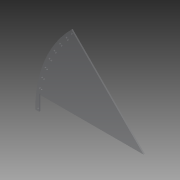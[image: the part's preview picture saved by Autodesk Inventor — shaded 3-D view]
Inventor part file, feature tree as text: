
AUTODESK INVENTOR PART (.ipt)
format: ipt  version: 2013 (Build 170138000, 138)  size: 107,520 bytes
history: native  units: in
note: dims shown in document units (in); Inventor stores cm internally (conversion verified against a paired STEP export)
features: extrude x2, sketch x2, reference x2
ambient origin geometry x8: Origin, YZ Plane, XZ Plane, XY Plane, X Axis, Y Axis, Z Axis, Center Point
feature tree (6):
  extrude  "Extrusion3"  Depth=0.375in
  extrude  "Extrusion5"  Depth=0.125in TaperAngle=0.0deg
  sketch  "Sketch3"  dims[d10=1.5in d12=0.375in]
  sketch  "Sketch4"  dims[d14=0.125in d15=0.0in d19=0.125in d20=0.0in]
  reference  "Reference1"
  reference  "Reference2"
